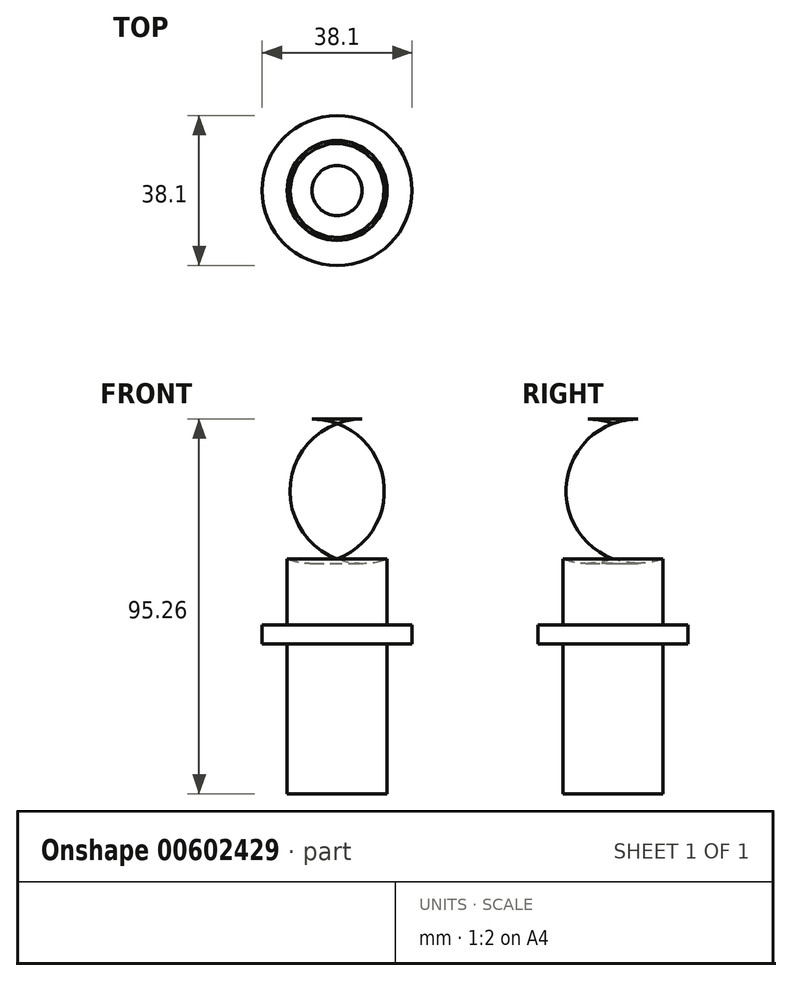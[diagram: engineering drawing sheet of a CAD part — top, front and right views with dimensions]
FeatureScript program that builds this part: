
annotation { "Feature Type Name" : "Feature", "Feature Type Description" : "" }
export const myFeature = defineFeature(function(context is Context, id is Id, definition is map)
    precondition{}
    {
        {
            var Q0;
            Q0=qCreatedBy(makeId("Front.planeOp"),FACE);
            var sketch = newSketch(context, id + "F0", { "sketchPlane" : qUnion([Q0])});
            skLineSegment(sketch, "E0", {"start": v(0, 47.63) * mm, "end": v(0, -47.63) * mm});
            skLineSegment(sketch, "E1", {"start": v(0, 47.63) * mm, "end": v(6.35, 47.63) * mm});
            skLineSegment(sketch, "E2", {"start": v(0, -47.63) * mm, "end": v(12.7, -47.63) * mm});
            skLineSegment(sketch, "E3", {"start": v(12.7, -47.63) * mm, "end": v(12.7, -9.53) * mm});
            skLineSegment(sketch, "E4", {"start": v(12.7, -9.53) * mm, "end": v(19.05, -9.53) * mm});
            skLineSegment(sketch, "E5", {"start": v(19.05, -9.53) * mm, "end": v(19.05, -4.75) * mm});
            skLineSegment(sketch, "E6", {"start": v(19.05, -4.75) * mm, "end": v(12.7, -4.75) * mm});
            skLineSegment(sketch, "E7", {"start": v(12.7, -4.75) * mm, "end": v(12.7, 12.12) * mm});
            skArc(sketch, "E8", {"start": v(6.35, 47.63) * mm, "mid": v(24.38, 32.53) * mm, "end": v(12.7, 12.12) * mm});
            skSolve(sketch);
        }
        {
            var Q0;
            Q0=makeQuery(id+"F0.imprint","IMPRINT",FACE,{"disambiguationData":[TD([[makeQuery(id+"F0.imprint","IMPRINT",EDGE,{"derivedFrom":sQuery(id+"F0.wireOp",EDGE,"E0")}),1.0]])]});
            var Q1;
            Q1=sQuery(id+"F0.wireOp",EDGE,"E0");
            revolve(context, id + "F1", {"entities" : qUnion([Q0]), "axis" : qUnion([Q1]), "revolveType" : RevolveType.FULL});
        }
    });
